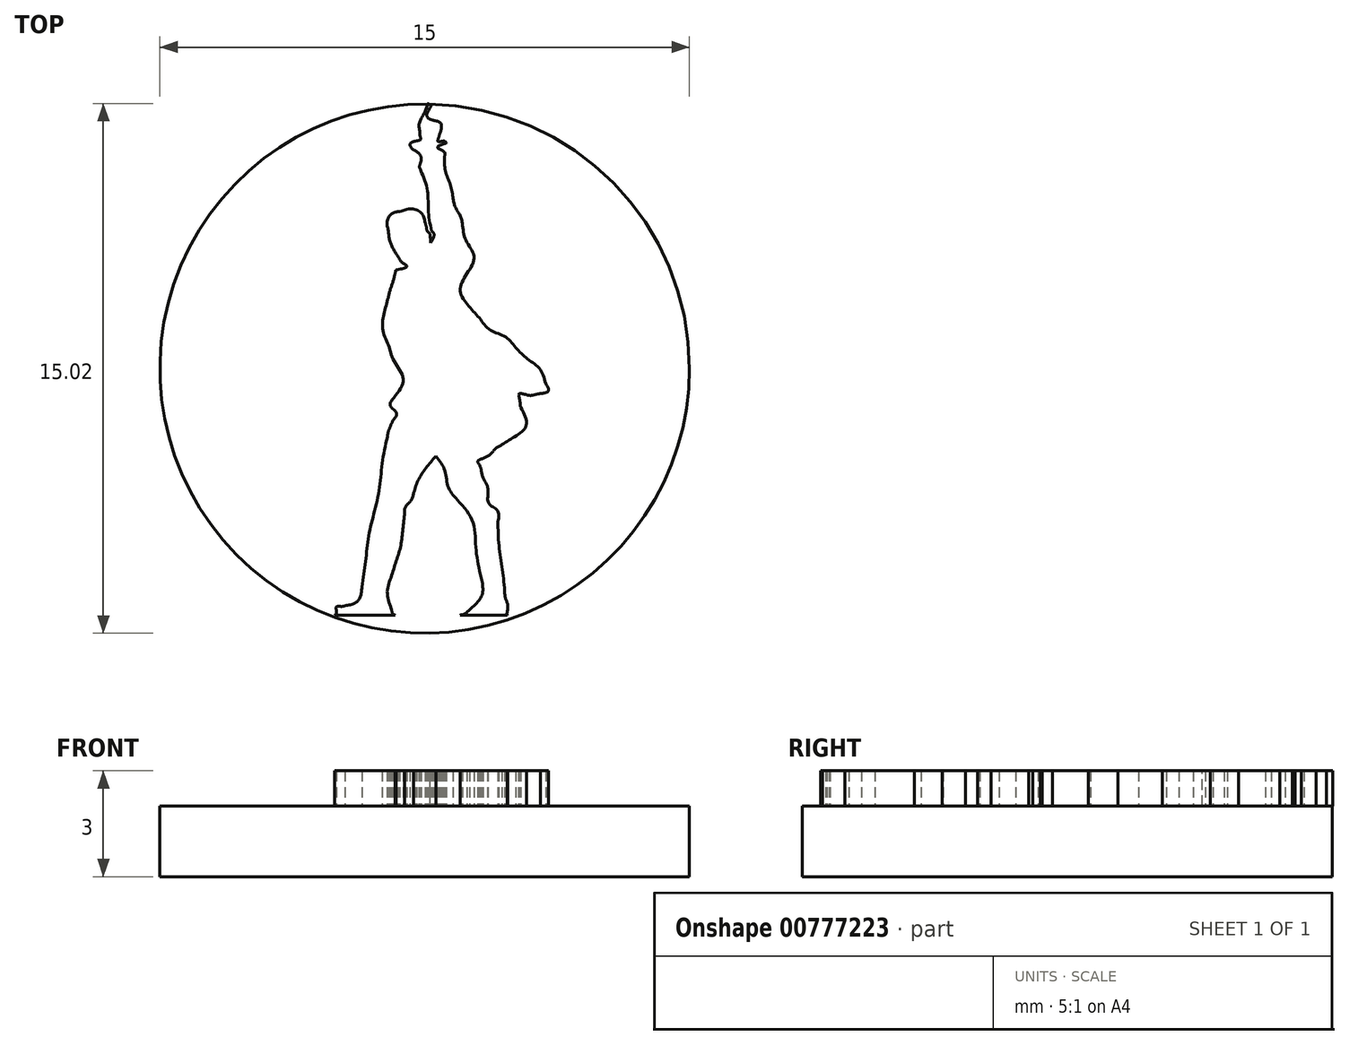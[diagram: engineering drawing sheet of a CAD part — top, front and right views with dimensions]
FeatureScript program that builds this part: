
annotation { "Feature Type Name" : "Feature", "Feature Type Description" : "" }
export const myFeature = defineFeature(function(context is Context, id is Id, definition is map)
    precondition{}
    {
        {
            var Q0;
            Q0=qCreatedBy(makeId("Top.planeOp"),FACE);
            var sketch = newSketch(context, id + "F0", { "sketchPlane" : qUnion([Q0])});
            skCircle(sketch, "E0", {"center": v(0, 0) * mm, "radius": 7.5 * mm});
            skSolve(sketch);
        }
        {
            var Q0;
            Q0=qCreatedBy(makeId("Top.planeOp"),FACE);
            var sketch = newSketch(context, id + "F1", { "sketchPlane" : qUnion([Q0])});
            skFitSpline(sketch, "E1", {"points": [v(-0.95, -6.8) * mm, v(-1.06, -6.33) * mm, v(-0.95, -5.9) * mm, v(-0.81, -5.45) * mm]});
            skFitSpline(sketch, "E2", {"points": [v(-0.81, -5.45) * mm, v(-0.68, -5.03) * mm, v(-0.62, -4.58) * mm, v(-0.57, -4.14) * mm]});
            skFitSpline(sketch, "E3", {"points": [v(-0.57, -4.14) * mm, v(-0.54, -3.91) * mm, v(-0.39, -3.74) * mm, v(-0.31, -3.52) * mm]});
            skFitSpline(sketch, "E4", {"points": [v(-0.31, -3.52) * mm, v(-0.18, -3.15) * mm, v(0.04, -2.8) * mm, v(0.32, -2.48) * mm]});
            skFitSpline(sketch, "E5", {"points": [v(0.32, -2.48) * mm, v(0.57, -2.88) * mm, v(0.66, -3.34) * mm, v(0.93, -3.72) * mm]});
            skFitSpline(sketch, "E6", {"points": [v(0.93, -3.72) * mm, v(1.36, -4.35) * mm, v(1.45, -5.1) * mm, v(1.58, -5.83) * mm]});
            skFitSpline(sketch, "E7", {"points": [v(1.58, -5.83) * mm, v(1.65, -6.24) * mm, v(1.57, -6.53) * mm, v(1.27, -6.83) * mm]});
            skFitSpline(sketch, "E8", {"points": [v(1.27, -6.83) * mm, v(1.17, -6.93) * mm, v(1.1, -6.97) * mm, v(1, -6.98) * mm]});
            skFitSpline(sketch, "E9", {"points": [v(2.34, -6.98) * mm, v(2.33, -6.97) * mm, v(2.33, -6.95) * mm, v(2.33, -6.93) * mm]});
            skFitSpline(sketch, "E10", {"points": [v(2.33, -6.93) * mm, v(2.35, -6.71) * mm, v(2.29, -6.5) * mm, v(2.26, -6.3) * mm]});
            skFitSpline(sketch, "E11", {"points": [v(2.26, -6.3) * mm, v(2.2, -5.64) * mm, v(2.1, -4.99) * mm, v(2.08, -4.33) * mm]});
            skFitSpline(sketch, "E12", {"points": [v(2.08, -4.33) * mm, v(2.06, -4.02) * mm, v(1.83, -3.84) * mm, v(1.8, -3.55) * mm]});
            skFitSpline(sketch, "E13", {"points": [v(1.8, -3.55) * mm, v(1.77, -3.32) * mm, v(1.66, -3.1) * mm, v(1.6, -2.88) * mm]});
            skFitSpline(sketch, "E14", {"points": [v(1.6, -2.88) * mm, v(1.57, -2.77) * mm, v(1.5, -2.63) * mm, v(1.65, -2.55) * mm]});
            skFitSpline(sketch, "E15", {"points": [v(1.65, -2.55) * mm, v(1.85, -2.44) * mm, v(2, -2.27) * mm, v(2.19, -2.16) * mm]});
            skFitSpline(sketch, "E16", {"points": [v(2.19, -2.16) * mm, v(2.58, -1.9) * mm, v(2.87, -1.62) * mm, v(2.72, -1.1) * mm]});
            skFitSpline(sketch, "E17", {"points": [v(2.72, -1.1) * mm, v(2.71, -1.06) * mm, v(2.71, -1.01) * mm, v(2.7, -0.97) * mm]});
            skFitSpline(sketch, "E18", {"points": [v(2.7, -0.97) * mm, v(2.68, -0.83) * mm, v(2.67, -0.72) * mm, v(2.89, -0.74) * mm]});
            skFitSpline(sketch, "E19", {"points": [v(2.89, -0.74) * mm, v(3.01, -0.76) * mm, v(3.15, -0.73) * mm, v(3.28, -0.7) * mm]});
            skFitSpline(sketch, "E20", {"points": [v(3.28, -0.7) * mm, v(3.44, -0.67) * mm, v(3.51, -0.62) * mm, v(3.43, -0.42) * mm]});
            skFitSpline(sketch, "E21", {"points": [v(3.43, -0.42) * mm, v(3.25, 0.01) * mm, v(2.9, 0.29) * mm, v(2.58, 0.6) * mm]});
            skFitSpline(sketch, "E22", {"points": [v(2.58, 0.6) * mm, v(2.26, 0.91) * mm, v(1.85, 1.1) * mm, v(1.55, 1.44) * mm]});
            skFitSpline(sketch, "E23", {"points": [v(1.55, 1.44) * mm, v(1.22, 1.8) * mm, v(1, 2.2) * mm, v(1.2, 2.7) * mm]});
            skFitSpline(sketch, "E24", {"points": [v(1.2, 2.7) * mm, v(1.4, 3.18) * mm, v(1.18, 3.61) * mm, v(1.07, 4.06) * mm]});
            skFitSpline(sketch, "E25", {"points": [v(1.07, 4.06) * mm, v(1, 4.33) * mm, v(0.87, 4.58) * mm, v(0.8, 4.86) * mm]});
            skFitSpline(sketch, "E26", {"points": [v(0.8, 4.86) * mm, v(0.71, 5.24) * mm, v(0.58, 5.63) * mm, v(0.57, 6.03) * mm]});
            skFitSpline(sketch, "E27", {"points": [v(0.57, 6.03) * mm, v(0.56, 6.14) * mm, v(0.37, 6.27) * mm, v(0.58, 6.38) * mm]});
            skFitSpline(sketch, "E28", {"points": [v(0.58, 6.38) * mm, v(0.61, 6.4) * mm, v(0.56, 6.45) * mm, v(0.52, 6.45) * mm]});
            skFitSpline(sketch, "E29", {"points": [v(0.52, 6.45) * mm, v(0.37, 6.45) * mm, v(0.38, 6.52) * mm, v(0.42, 6.63) * mm]});
            skFitSpline(sketch, "E30", {"points": [v(0.42, 6.63) * mm, v(0.47, 6.8) * mm, v(0.45, 6.96) * mm, v(0.24, 7.04) * mm]});
            skFitSpline(sketch, "E31", {"points": [v(0.24, 7.04) * mm, v(0.1, 7.1) * mm, v(0.06, 7.2) * mm, v(0.12, 7.34) * mm]});
            skFitSpline(sketch, "E32", {"points": [v(0.12, 7.34) * mm, v(0.14, 7.39) * mm, v(0.18, 7.45) * mm, v(0.08, 7.52) * mm]});
            skFitSpline(sketch, "E33", {"points": [v(0.08, 7.52) * mm, v(-0.01, 7.24) * mm, v(-0.15, 6.98) * mm, v(-0.13, 6.7) * mm]});
            skFitSpline(sketch, "E34", {"points": [v(-0.13, 6.7) * mm, v(-0.13, 6.57) * mm, v(-0.11, 6.5) * mm, v(-0.23, 6.45) * mm]});
            skFitSpline(sketch, "E35", {"points": [v(-0.23, 6.45) * mm, v(-0.4, 6.38) * mm, v(-0.39, 6.27) * mm, v(-0.27, 6.18) * mm]});
            skFitSpline(sketch, "E36", {"points": [v(-0.27, 6.18) * mm, v(-0.14, 6.07) * mm, v(-0.1, 5.94) * mm, v(-0.14, 5.78) * mm]});
            skFitSpline(sketch, "E37", {"points": [v(-0.14, 5.78) * mm, v(-0.15, 5.72) * mm, v(-0.13, 5.67) * mm, v(-0.11, 5.62) * mm]});
            skFitSpline(sketch, "E38", {"points": [v(-0.11, 5.62) * mm, v(0.08, 5.07) * mm, v(0.1, 4.48) * mm, v(0.2, 3.91) * mm]});
            skFitSpline(sketch, "E39", {"points": [v(0.2, 3.91) * mm, v(0.26, 3.82) * mm, v(0.25, 3.73) * mm, v(0.17, 3.57) * mm]});
            skFitSpline(sketch, "E40", {"points": [v(0.17, 3.57) * mm, v(0.16, 3.7) * mm, v(0.16, 3.76) * mm, v(0.15, 3.82) * mm]});
            skFitSpline(sketch, "E41", {"points": [v(0.15, 3.82) * mm, v(0.07, 3.9) * mm, v(0.05, 4.02) * mm, v(0, 4.13) * mm]});
            skFitSpline(sketch, "E42", {"points": [v(0, 4.13) * mm, v(-0.08, 4.4) * mm, v(-0.38, 4.53) * mm, v(-0.7, 4.45) * mm]});
            skFitSpline(sketch, "E43", {"points": [v(-0.7, 4.45) * mm, v(-0.92, 4.4) * mm, v(-1.06, 4.17) * mm, v(-1.03, 3.91) * mm]});
            skFitSpline(sketch, "E44", {"points": [v(-1.03, 3.91) * mm, v(-1, 3.64) * mm, v(-0.89, 3.39) * mm, v(-0.74, 3.16) * mm]});
            skFitSpline(sketch, "E45", {"points": [v(-0.74, 3.16) * mm, v(-0.66, 3.02) * mm, v(-0.5, 2.9) * mm, v(-0.78, 2.8) * mm]});
            skFitSpline(sketch, "E46", {"points": [v(-0.78, 2.8) * mm, v(-0.81, 2.8) * mm, v(-0.83, 2.72) * mm, v(-0.84, 2.68) * mm]});
            skFitSpline(sketch, "E47", {"points": [v(-0.84, 2.68) * mm, v(-0.9, 2.46) * mm, v(-0.98, 2.24) * mm, v(-1.03, 2.02) * mm]});
            skFitSpline(sketch, "E48", {"points": [v(-1.03, 2.02) * mm, v(-1.15, 1.56) * mm, v(-1.2, 1.13) * mm, v(-1.03, 0.67) * mm]});
            skFitSpline(sketch, "E49", {"points": [v(-1.03, 0.67) * mm, v(-0.85, 0.19) * mm, v(-0.6, -0.3) * mm, v(-0.87, -0.82) * mm]});
            skFitSpline(sketch, "E50", {"points": [v(-0.87, -0.82) * mm, v(-0.98, -1.04) * mm, v(-0.8, -1.25) * mm, v(-0.9, -1.46) * mm]});
            skFitSpline(sketch, "E51", {"points": [v(-0.9, -1.46) * mm, v(-0.97, -1.61) * mm, v(-1.03, -1.77) * mm, v(-1.06, -1.93) * mm]});
            skFitSpline(sketch, "E52", {"points": [v(-1.06, -1.93) * mm, v(-1.2, -2.66) * mm, v(-1.28, -3.4) * mm, v(-1.44, -4.12) * mm]});
            skFitSpline(sketch, "E53", {"points": [v(-1.44, -4.12) * mm, v(-1.6, -4.8) * mm, v(-1.68, -5.5) * mm, v(-1.78, -6.18) * mm]});
            skFitSpline(sketch, "E54", {"points": [v(-1.78, -6.18) * mm, v(-1.82, -6.47) * mm, v(-1.98, -6.64) * mm, v(-2.25, -6.72) * mm]});
            skFitSpline(sketch, "E55", {"points": [v(-2.25, -6.72) * mm, v(-2.35, -6.74) * mm, v(-2.5, -6.75) * mm, v(-2.5, -6.85) * mm]});
            skFitSpline(sketch, "E56", {"points": [v(-2.5, -6.85) * mm, v(-2.5, -6.93) * mm, v(-2.52, -6.97) * mm, v(-2.55, -6.98) * mm]});
            skLineSegment(sketch, "E57", {"start": v(1, -6.98) * mm, "end": v(2.34, -6.98) * mm});
            skFitSpline(sketch, "E58", {"points": [v(-0.84, -6.98) * mm, v(-0.9, -6.96) * mm, v(-0.92, -6.9) * mm, v(-0.95, -6.8) * mm]});
            skLineSegment(sketch, "E59", {"start": v(-2.55, -6.98) * mm, "end": v(-0.84, -6.98) * mm});
            skSolve(sketch);
        }
        {
            var Q0;
            Q0 = qSketchRegion(id + "F0", true);
            extrude(context, id + "F2", {"entities" : qUnion([Q0]), "oppositeDirection" : true, "depth" : 2 * mm, "offsetDistance" : 25 * mm});
        }
        {
            var Q0;
            Q0 = qSketchRegion(id + "F1", true);
            extrude(context, id + "F3", {"entities" : qUnion([Q0]), "operationType" : NewBodyOperationType.ADD, "depth" : 1 * mm, "offsetDistance" : 25 * mm});
        }
    });
